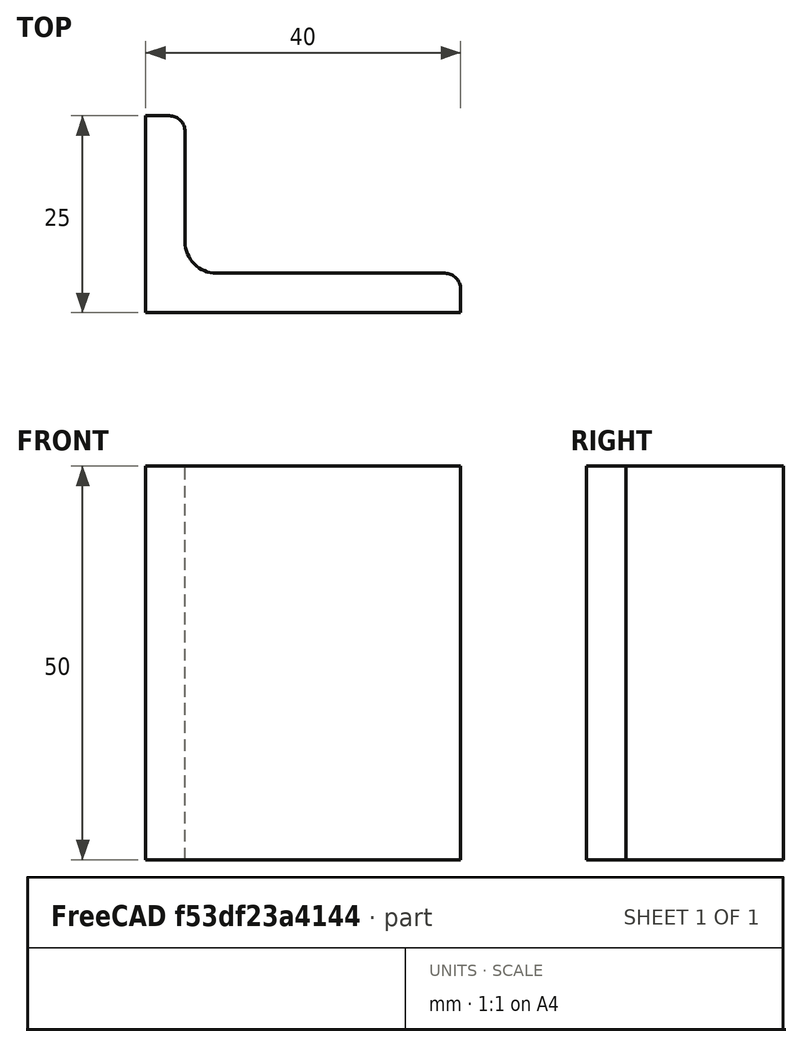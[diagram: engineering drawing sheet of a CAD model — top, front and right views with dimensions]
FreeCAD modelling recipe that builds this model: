
FCSTD DOCUMENT  (FreeCAD 0.15R4671 (Git))
Label: Angle Bar 40x25x5 EN10056 S235JR
License: All rights reserved
LicenseURL: http://en.wikipedia.org/wiki/All_rights_reserved
objects: Sketcher::SketchObject×1, Part::Extrusion×1
note: 2 computed .brp shape members not serialized (recipe doc carries the construction recipe); baked Part::Feature solids carry a one-line shape summary decoded from their .brp

FEATURE [Sketcher::SketchObject] Sketch
  sketch-geometry (9):
    g0: LineSegment StartX=0 StartY=0 StartZ=0 EndX=40 EndY=0 EndZ=0
    g1: LineSegment StartX=40 StartY=0 StartZ=0 EndX=40 EndY=3 EndZ=0
    g2: LineSegment StartX=38 StartY=5 StartZ=0 EndX=9 EndY=5 EndZ=0
    g3: LineSegment StartX=0 StartY=0 StartZ=0 EndX=0 EndY=25 EndZ=0
    g4: LineSegment StartX=0 StartY=25 StartZ=0 EndX=3 EndY=25 EndZ=0
    g5: LineSegment StartX=5 StartY=23 StartZ=0 EndX=5 EndY=9 EndZ=0
    g6: ArcOfCircle CenterX=9 CenterY=9 CenterZ=0 NormalX=0 NormalY=0 NormalZ=1 Radius=4 StartAngle=3.14159 EndAngle=4.71239
    g7: ArcOfCircle CenterX=3 CenterY=23 CenterZ=0 NormalX=0 NormalY=0 NormalZ=1 Radius=2 StartAngle=0 EndAngle=1.5708
    g8: ArcOfCircle CenterX=38 CenterY=3 CenterZ=0 NormalX=0 NormalY=0 NormalZ=1 Radius=2 StartAngle=0 EndAngle=1.5708
  constraints (23):
    c: Coincident(g0,g-1)
    c: Horizontal(g0)
    c: Coincident(g1,g0)
    c: Vertical(g1)
    c: Horizontal(g2)
    c: Coincident(g3,g-1)
    c: Vertical(g3)
    c: Coincident(g4,g3)
    c: Horizontal(g4)
    c: Vertical(g5)
    c: Tangent(g5,g6) = -1.5708
    c: Tangent(g2,g6) = 1.5708
    c: Tangent(g4,g7) = 1.5708
    c: Tangent(g5,g7) = 1.5708
    c: Tangent(g2,g8) = -1.5708
    c: Tangent(g1,g8) = -1.5708
    c: DistanceX(g0) = 40
    c: DistanceY(g3) = 25
    c: DistanceY(g0,g2) = 5
    c: DistanceX(g3,g5) = 5
    c: Radius(g6) = 4
    c: Radius(g8) = 2
    c: Radius(g7) = 2
FEATURE [Part::Extrusion] Extrude  label="Angle Bar 40x25x5 EN10056 S235JR"
  Base = -> Sketch
  Dir = (0,0,50)
  Solid = true
